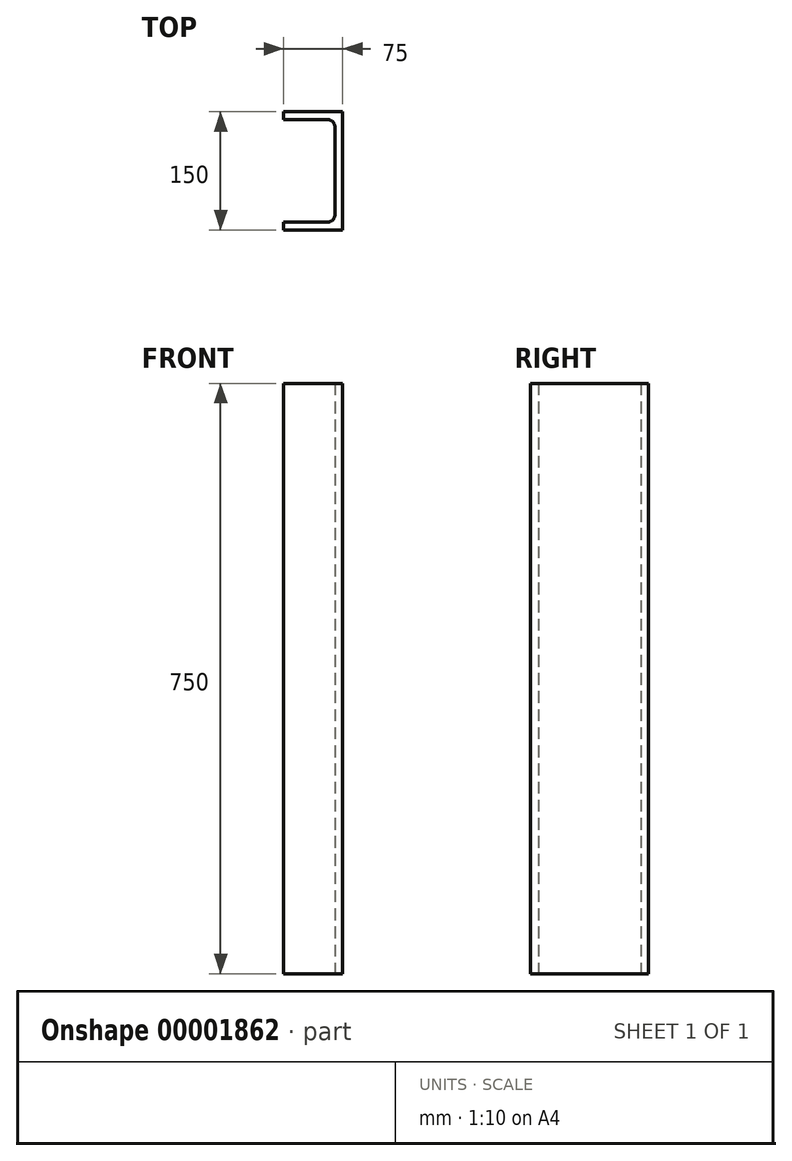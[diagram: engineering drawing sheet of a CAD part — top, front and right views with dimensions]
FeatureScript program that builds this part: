
annotation { "Feature Type Name" : "Feature", "Feature Type Description" : "" }
export const myFeature = defineFeature(function(context is Context, id is Id, definition is map)
    precondition{}
    {
        {
            var Q0;
            Q0=qCreatedBy(makeId("Top.planeOp"),FACE);
            var sketch = newSketch(context, id + "F0", { "sketchPlane" : qUnion([Q0])});
            skLineSegment(sketch, "E0", {"start": v(0, 0) * mm, "end": v(0, 150) * mm});
            skLineSegment(sketch, "E1", {"start": v(0, 150) * mm, "end": v(-75, 150) * mm});
            skLineSegment(sketch, "E2", {"start": v(-75, 150) * mm, "end": v(-75, 140) * mm});
            skLineSegment(sketch, "E3", {"start": v(-75, 140) * mm, "end": v(-19, 140) * mm});
            skLineSegment(sketch, "E4", {"start": v(-10, 131) * mm, "end": v(-10, 19) * mm});
            skLineSegment(sketch, "E5", {"start": v(-19, 10) * mm, "end": v(-75, 10) * mm});
            skLineSegment(sketch, "E6", {"start": v(-75, 10) * mm, "end": v(-75, 0) * mm});
            skLineSegment(sketch, "E7", {"start": v(-75, 0) * mm, "end": v(0, 0) * mm});
            skPoint(sketch, "E8.visualSharp", {"position": v(-10, 140) * mm});
            skArc(sketch, "E8.filletArc", {"start": v(-10, 131) * mm, "mid": v(-12.64, 137.36) * mm, "end": v(-19, 140) * mm});
            skPoint(sketch, "E9.visualSharp", {"position": v(-10, 10) * mm});
            skArc(sketch, "E9.filletArc", {"start": v(-19, 10) * mm, "mid": v(-12.64, 12.64) * mm, "end": v(-10, 19) * mm});
            skLineSegment(sketch, "E10", {"start": v(0, 75) * mm, "end": v(-122.59, 75) * mm, "construction": true});
            skSolve(sketch);
        }
        {
            var Q0;
            Q0=makeQuery(id+"F0.imprint","IMPRINT",FACE,{"disambiguationData":[TD([[makeQuery(id+"F0.imprint","IMPRINT",EDGE,{"derivedFrom":sQuery(id+"F0.wireOp",EDGE,"E0")}),1.0]])]});
            extrude(context, id + "F1", {"entities" : qUnion([Q0]), "depth" : 750 * mm});
        }
    });
